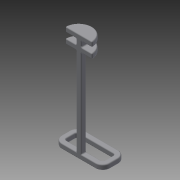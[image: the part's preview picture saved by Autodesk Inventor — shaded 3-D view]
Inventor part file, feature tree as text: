
AUTODESK INVENTOR PART (.ipt)
format: ipt  version: 2014 (Build 180170000, 170)  size: 332,800 bytes
history: native  units: mm
features: extrude x4, fillet x4, sketch x4
ambient origin geometry x8: Origin, YZ Plane, XZ Plane, XY Plane, X Axis, Y Axis, Z Axis, Center Point
bodies: Solid1 (feature_tree)
feature tree (12):
  extrude  "Extrusion1"  Depth=5.0mm
  extrude  "Extrusion2"  Depth=37.0mm
  extrude  "Extrusion6"  Depth=5.0mm
  extrude  "Extrusion7"  Depth=2.0mm
  fillet  "Fillet1"  Radius=13.0mm
  fillet  "Fillet2"  Radius=15.0mm
  fillet  "Fillet3"  Radius=5.0mm
  fillet  "Fillet4"  Radius=5.0mm
  sketch  "Sketch1"  dims[d0=5.0mm d1=5.0mm]
  sketch  "Sketch2"  dims[d2=12.0mm d3=37.0mm]
  sketch  "Sketch7"  dims[d4=5.0mm d5=0.0mm d6=5.0mm]
  sketch  "Sketch8"  dims[d7=85.0mm d8=0.0mm d19=2.0mm d23=13.0mm d24=15.0mm d25=0.0mm d26=5.0mm d27=5.0mm d28=0.0mm d29=0.0mm d30=1.0mm d31=1.0mm d32=1.0mm d33=1.0mm]
